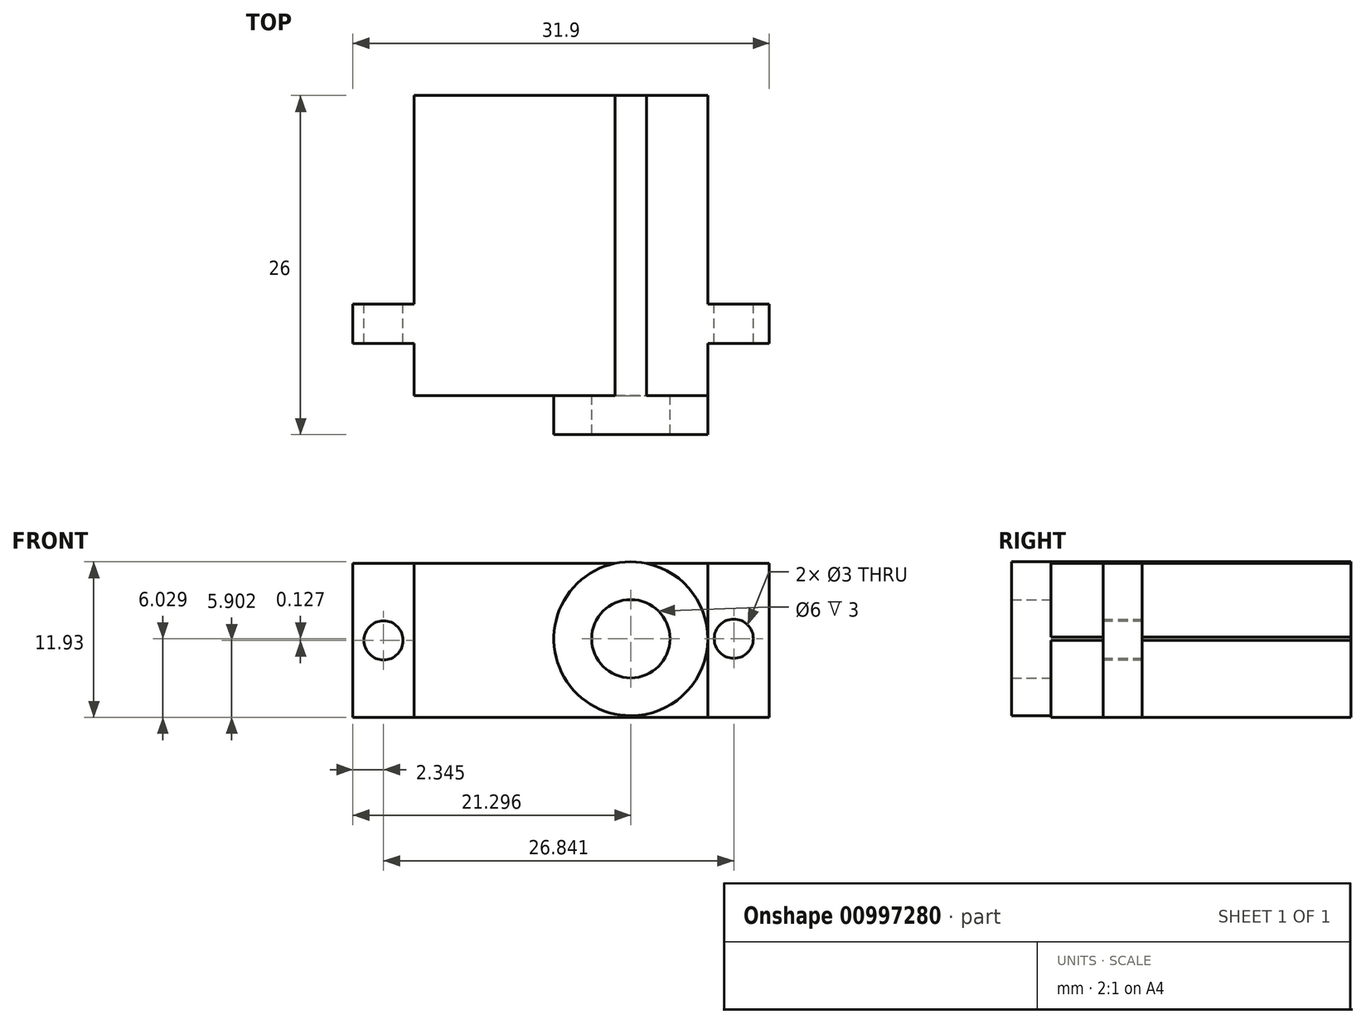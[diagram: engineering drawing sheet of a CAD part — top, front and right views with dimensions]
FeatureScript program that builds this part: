
annotation { "Feature Type Name" : "Feature", "Feature Type Description" : "" }
export const myFeature = defineFeature(function(context is Context, id is Id, definition is map)
    precondition{}
    {
        {
            var Q0;
            Q0=qCreatedBy(makeId("Front.planeOp"),FACE);
            var sketch = newSketch(context, id + "F0", { "sketchPlane" : qUnion([Q0])});
            skLineSegment(sketch, "E0.bottom", {"start": v(-45.43, 30.95) * mm, "end": v(-22.93, 30.95) * mm});
            skLineSegment(sketch, "E0.top", {"start": v(-45.43, 19.15) * mm, "end": v(-22.93, 19.15) * mm});
            skLineSegment(sketch, "E0.left", {"start": v(-45.43, 30.95) * mm, "end": v(-45.43, 19.15) * mm});
            skLineSegment(sketch, "E0.right", {"start": v(-22.93, 30.95) * mm, "end": v(-22.93, 19.15) * mm});
            skSolve(sketch);
        }
        {
            var Q0;
            Q0=qCreatedBy(makeId("Front.planeOp"),FACE);
            var sketch = newSketch(context, id + "F1", { "sketchPlane" : qUnion([Q0])});
            skCircle(sketch, "E1", {"center": v(-28.83, 25.18) * mm, "radius": 5.9 * mm});
            skCircle(sketch, "E2", {"center": v(-28.83, 25.18) * mm, "radius": 3 * mm});
            skSolve(sketch);
        }
        {
            var Q0;
            Q0 = qSketchRegion(id + "F0", true);
            extrude(context, id + "F2", {"entities" : qUnion([Q0]), "depth" : 23 * mm, "offsetDistance" : 25 * mm});
        }
        {
            var Q0;
            Q0 = qSketchRegion(id + "F1", true);
            extrude(context, id + "F3", {"entities" : qUnion([Q0]), "operationType" : NewBodyOperationType.ADD, "depth" : 26 * mm, "offsetDistance" : 25 * mm});
        }
        {
            var Q0;
            Q0=qCreatedBy(makeId("Front.planeOp"),FACE);
            var sketch = newSketch(context, id + "F4", { "sketchPlane" : qUnion([Q0])});
            skLineSegment(sketch, "E3.bottom", {"start": v(-22.93, 30.95) * mm, "end": v(-18.23, 30.95) * mm});
            skLineSegment(sketch, "E3.top", {"start": v(-22.93, 19.15) * mm, "end": v(-18.23, 19.15) * mm});
            skLineSegment(sketch, "E3.left", {"start": v(-22.93, 31.15) * mm, "end": v(-22.93, 19.15) * mm});
            skLineSegment(sketch, "E3.right", {"start": v(-18.23, 30.95) * mm, "end": v(-18.23, 19.15) * mm});
            skCircle(sketch, "E4", {"center": v(-20.94, 25.18) * mm, "radius": 1.5 * mm});
            skLineSegment(sketch, "E5.bottom", {"start": v(-45.43, 19.15) * mm, "end": v(-50.13, 19.15) * mm});
            skLineSegment(sketch, "E5.top", {"start": v(-45.43, 30.95) * mm, "end": v(-50.13, 30.95) * mm});
            skLineSegment(sketch, "E5.left", {"start": v(-45.43, 19.15) * mm, "end": v(-45.43, 30.95) * mm});
            skLineSegment(sketch, "E5.right", {"start": v(-50.13, 19.15) * mm, "end": v(-50.13, 30.95) * mm});
            skPoint(sketch, "E5.middle", {"position": v(-47.78, 25.05) * mm});
            skCircle(sketch, "E6", {"center": v(-47.78, 25.05) * mm, "radius": 1.5 * mm});
            skSolve(sketch);
        }
        {
            var Q0;
            Q0=makeQuery(id+"F4.imprint","IMPRINT",FACE,{"disambiguationData":[TD([[makeQuery(id+"F4.imprint","IMPRINT",EDGE,{"derivedFrom":sQuery(id+"F4.wireOp",EDGE,"E3.bottom")}),-1.0]])]});
            extrude(context, id + "F5", {"entities" : qUnion([Q0]), "operationType" : NewBodyOperationType.ADD, "depth" : 19 * mm, "offsetDistance" : 25 * mm, "hasSecondDirection" : true, "secondDirectionOppositeDirection" : false, "secondDirectionDepth" : 16 * mm});
        }
        {
            var Q0;
            Q0=makeQuery(id+"F4.imprint","IMPRINT",FACE,{"disambiguationData":[TD([[makeQuery(id+"F4.imprint","IMPRINT",EDGE,{"derivedFrom":sQuery(id+"F4.wireOp",EDGE,"E5.bottom")}),-1.0]])]});
            extrude(context, id + "F6", {"entities" : qUnion([Q0]), "operationType" : NewBodyOperationType.ADD, "depth" : 19 * mm, "offsetDistance" : 25 * mm, "hasSecondDirection" : true, "secondDirectionOppositeDirection" : false, "secondDirectionDepth" : 16 * mm});
        }
    });
